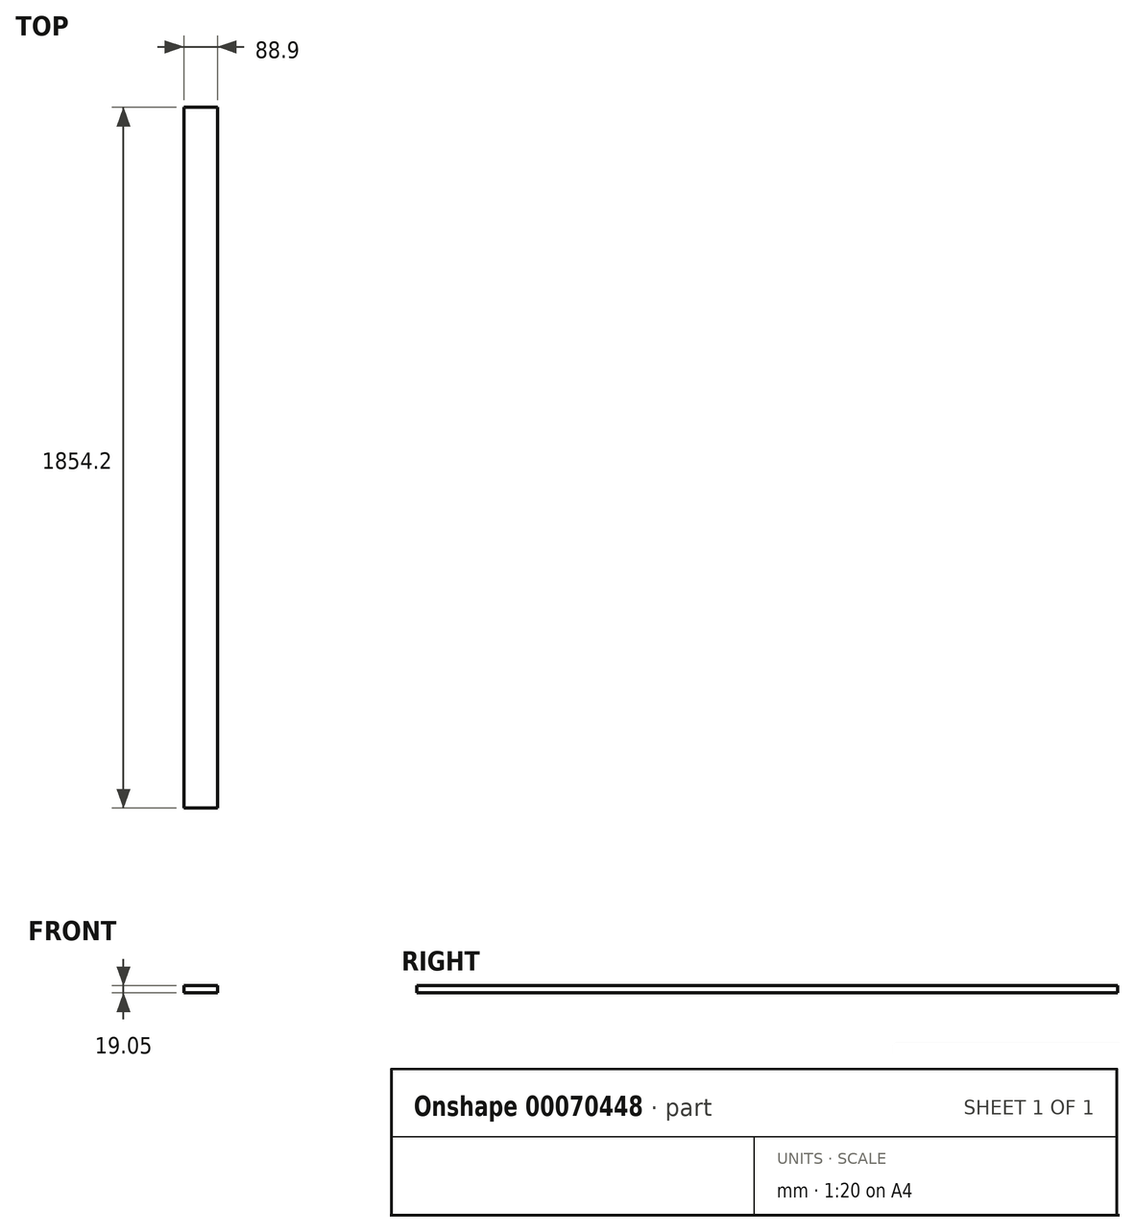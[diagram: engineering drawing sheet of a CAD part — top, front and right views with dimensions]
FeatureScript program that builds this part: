
annotation { "Feature Type Name" : "Feature", "Feature Type Description" : "" }
export const myFeature = defineFeature(function(context is Context, id is Id, definition is map)
    precondition{}
    {
        {
            var Q0;
            Q0=qCreatedBy(makeId("Front.planeOp"),FACE);
            var sketch = newSketch(context, id + "F0", { "sketchPlane" : qUnion([Q0])});
            skLineSegment(sketch, "E0.bottom", {"start": v(92.27, 136.6) * mm, "end": v(181.17, 136.6) * mm});
            skLineSegment(sketch, "E0.top", {"start": v(92.27, 117.56) * mm, "end": v(181.17, 117.56) * mm});
            skLineSegment(sketch, "E0.left", {"start": v(92.27, 136.6) * mm, "end": v(92.27, 117.56) * mm});
            skLineSegment(sketch, "E0.right", {"start": v(181.17, 136.6) * mm, "end": v(181.17, 117.56) * mm});
            skSolve(sketch);
        }
        {
            var Q0;
            Q0 = qSketchRegion(id + "F0", true);
            extrude(context, id + "F1", {"entities" : qUnion([Q0]), "oppositeDirection" : true, "depth" : 1854.2 * mm});
        }
    });
